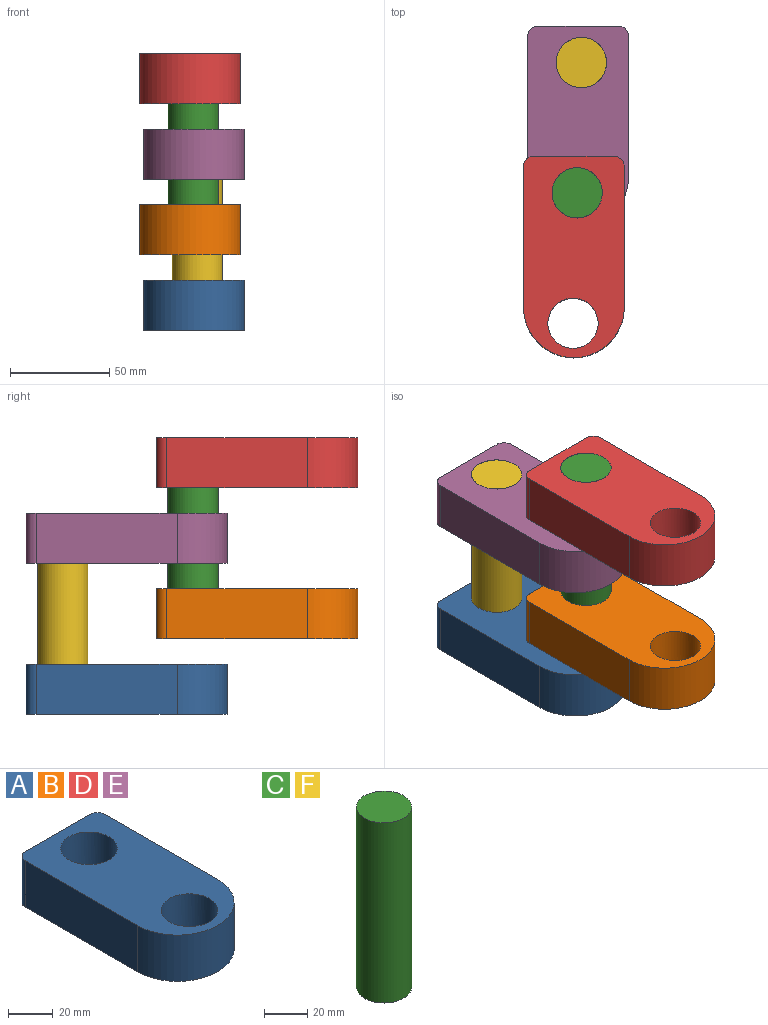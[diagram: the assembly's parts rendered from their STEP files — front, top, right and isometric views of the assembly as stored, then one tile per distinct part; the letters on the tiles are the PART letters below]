
ASSEMBLY  parts=6 mates=4
PART A: 10 faces, bbox 50.8x101.6x25.4 mm
  f0: plane 71.12x25.4mm, normal (1,0,0), area 1806.4mm2, adj f3,f4,f7,f8
  f1: plane 40.64x25.4mm, normal (0,1,0), area 1032.3mm2, adj f3,f4,f8,f9
  f2: plane 71.12x25.4mm, normal (-1,0,0), area 1806.4mm2, adj f3,f4,f7,f9
  f3: plane 101.6x50.8mm, normal (0,0,1), area 3859.9mm2, adj f0,f1,f2,f5,f6,f7,f8,f9
  f4: plane 101.6x50.8mm, normal (0,0,-1), area 3859.9mm2, adj f0,f1,f2,f5,f6,f7,f8,f9
  f5: cylinder r=12.7mm len=25.4mm, axis (0,0,-1), area 2026.8mm2, adj f3,f4
  f6: cylinder r=12.7mm len=25.4mm, axis (0,0,-1), area 2026.8mm2, adj f3,f4
  f7: cylinder r=25.4mm len=50.8mm, axis (0,0,-1), area 2026.8mm2, adj f0,f2,f3,f4
  f8: cylinder r=5.08mm len=25.4mm, axis (0,0,-1), area 202.7mm2, adj f0,f1,f3,f4
  f9: cylinder r=5.08mm len=25.4mm, axis (0,0,-1), area 202.7mm2, adj f1,f2,f3,f4
PART B: same geometry as A
PART C: 3 faces, bbox 25.4x25.4x101.6 mm
  f0: cylinder r=12.7mm len=101.6mm, axis (0,0,-1), area 8107.3mm2, adj f1,f2
  f1: plane 25.4x25.4mm, normal (0,0,1), area 506.7mm2, adj f0
  f2: plane 25.4x25.4mm, normal (0,0,-1), area 506.7mm2, adj f0
PART D: same geometry as A
PART E: same geometry as A
PART F: same geometry as C
PLACE A t=(130.91,157.91,-71.69)mm
PLACE B t=(128.81,92.08,-33.59)mm
PLACE C t=(103.64,91.3,-33.59)mm
PLACE D t=(128.81,92.08,42.61)mm
PLACE E t=(130.91,157.91,4.51)mm
PLACE F t=(105.74,157.12,-71.69)mm
MATE revolute F.f0 <-> E.f6  axis (0,0,1) through (137.74,188.12,29.91)mm
MATE revolute D.f6 <-> C.f0  axis (0,0,-1) through (135.64,122.3,68.01)mm
MATE revolute B.f6 <-> C.f0  axis (0,0,-1) through (135.64,122.3,-33.59)mm
MATE revolute A.f6 <-> F.f0  axis (0,0,-1) through (137.74,188.12,-71.69)mm
